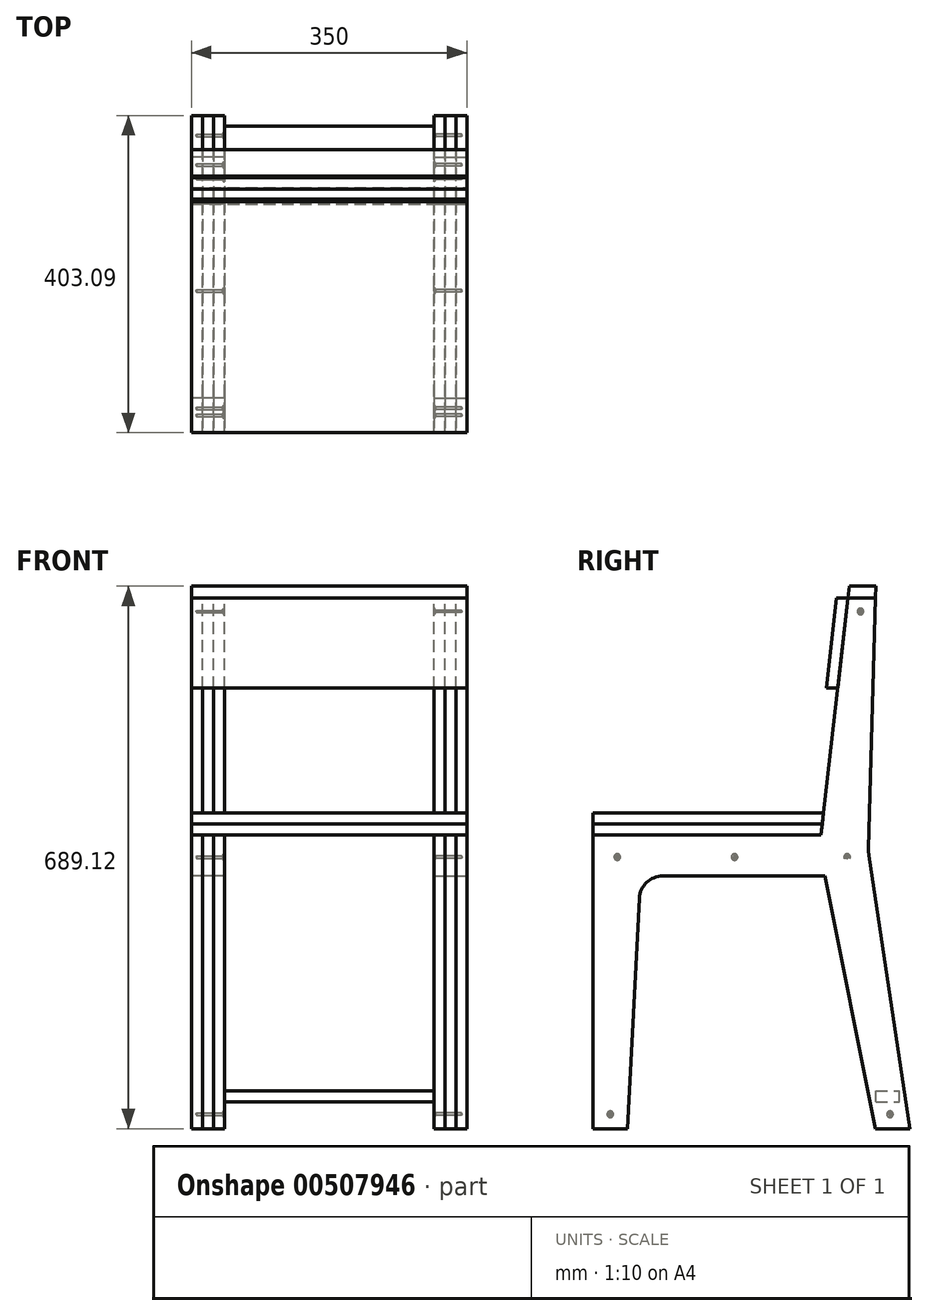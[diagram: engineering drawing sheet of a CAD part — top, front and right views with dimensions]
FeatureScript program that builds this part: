
annotation { "Feature Type Name" : "Feature", "Feature Type Description" : "" }
export const myFeature = defineFeature(function(context is Context, id is Id, definition is map)
    precondition{}
    {
        {
            var Q0;
            Q0=qCreatedBy(makeId("Right.planeOp"),FACE);
            var sketch = newSketch(context, id + "F0", { "sketchPlane" : qUnion([Q0])});
            skLineSegment(sketch, "E0", {"start": v(-65.3, 0) * mm, "end": v(224.7, 0) * mm});
            skLineSegment(sketch, "E1", {"start": v(224.7, 0) * mm, "end": v(258.7, 301.28) * mm});
            skLineSegment(sketch, "E2", {"start": v(258.7, 301.28) * mm, "end": v(293.7, 301.28) * mm});
            skLineSegment(sketch, "E3", {"start": v(337.7, -373) * mm, "end": v(293.7, -373) * mm});
            skLineSegment(sketch, "E4", {"start": v(293.7, -373) * mm, "end": v(229.2, -52) * mm});
            skLineSegment(sketch, "E5", {"start": v(229.2, -52) * mm, "end": v(23.69, -52) * mm});
            skLineSegment(sketch, "E6", {"start": v(-21.3, -373) * mm, "end": v(-65.3, -373) * mm});
            skLineSegment(sketch, "E7", {"start": v(-65.3, -373) * mm, "end": v(-65.3, 0) * mm});
            skPoint(sketch, "E8.visualSharp", {"position": v(-29.5, -52) * mm});
            skLineSegment(sketch, "E9.bottom", {"start": v(-65.3, 0) * mm, "end": v(-29.5, 0) * mm});
            skLineSegment(sketch, "E9.top", {"start": v(-65.3, -373) * mm, "end": v(-21.3, -373) * mm});
            skLineSegment(sketch, "E9.left", {"start": v(-65.3, 0) * mm, "end": v(-65.3, -373) * mm});
            skLineSegment(sketch, "E10", {"start": v(337.7, -373) * mm, "end": v(285.36, -25.8) * mm});
            skLineSegment(sketch, "E11", {"start": v(284.82, -16.95) * mm, "end": v(293.7, 301.28) * mm});
            skLineSegment(sketch, "E12", {"start": v(-6.27, -80.46) * mm, "end": v(-21.3, -373) * mm});
            skPoint(sketch, "E13.visualSharp", {"position": v(-4.8, -52) * mm});
            skArc(sketch, "E13.filletArc", {"start": v(23.69, -52) * mm, "mid": v(3.03, -60.25) * mm, "end": v(-6.27, -80.46) * mm});
            skPoint(sketch, "E14.visualSharp", {"position": v(284.7, -21.4) * mm});
            skArc(sketch, "E14.filletArc", {"start": v(284.82, -16.95) * mm, "mid": v(284.89, -21.38) * mm, "end": v(285.36, -25.8) * mm});
            skSolve(sketch);
        }
        {
            var Q0;
            Q0=qCreatedBy(makeId("Right.planeOp"),FACE);
            var sketch = newSketch(context, id + "F1", { "sketchPlane" : qUnion([Q0])});
            skLineSegment(sketch, "E15", {"start": v(-65.3, 0) * mm, "end": v(224.7, 0) * mm});
            skLineSegment(sketch, "E16", {"start": v(224.7, 0) * mm, "end": v(226.27, 14) * mm});
            skLineSegment(sketch, "E17", {"start": v(226.27, 14) * mm, "end": v(-65.3, 14) * mm});
            skLineSegment(sketch, "E18", {"start": v(-65.3, 14) * mm, "end": v(-65.3, 0) * mm});
            skSolve(sketch);
        }
        {
            var Q0;
            Q0=qCreatedBy(makeId("Right.planeOp"),FACE);
            var sketch = newSketch(context, id + "F2", { "sketchPlane" : qUnion([Q0])});
            skLineSegment(sketch, "E19", {"start": v(-65.3, 14) * mm, "end": v(226.27, 14) * mm});
            skLineSegment(sketch, "E20", {"start": v(226.27, 14) * mm, "end": v(227.85, 28) * mm});
            skLineSegment(sketch, "E21", {"start": v(227.85, 28) * mm, "end": v(-65.4, 28) * mm});
            skLineSegment(sketch, "E22", {"start": v(-65.4, 28) * mm, "end": v(-65.3, 14) * mm});
            skSolve(sketch);
        }
        {
            var Q0;
            Q0=makeQuery(id+"F0.imprint","IMPRINT",FACE,{"disambiguationData":[TD([[makeQuery(id+"F0.imprint","IMPRINT",EDGE,{"derivedFrom":sQuery(id+"F0.wireOp",EDGE,"E0")}),-1.0]])]});
            extrude(context, id + "F3", {"entities" : qUnion([Q0]), "oppositeDirection" : true, "depth" : 14 * mm});
        }
        {
            var Q0;
            Q0=makeQuery(id+"F1.imprint","IMPRINT",FACE,{"disambiguationData":[TD([[makeQuery(id+"F1.imprint","IMPRINT",EDGE,{"derivedFrom":sQuery(id+"F1.wireOp",EDGE,"E15")}),1.0]])]});
            extrude(context, id + "F4", {"entities" : qUnion([Q0]), "oppositeDirection" : true, "depth" : 350 * mm});
        }
        {
            var Q0;
            Q0=makeQuery(id+"F3.opExtrude","SWEPT_BODY",BODY,{"disambiguationData":[OSD([sQuery(id+"F0.wireOp",EDGE,"E0"),sQuery(id+"F0.wireOp",EDGE,"E1"),sQuery(id+"F0.wireOp",EDGE,"E2"),sQuery(id+"F0.wireOp",EDGE,"E3"),sQuery(id+"F0.wireOp",EDGE,"E4"),sQuery(id+"F0.wireOp",EDGE,"E5"),sQuery(id+"F0.wireOp",EDGE,"E9.bottom"),sQuery(id+"F0.wireOp",EDGE,"E9.top"),sQuery(id+"F0.wireOp",EDGE,"E9.left"),sQuery(id+"F0.wireOp",EDGE,"E10"),sQuery(id+"F0.wireOp",EDGE,"E11"),sQuery(id+"F0.wireOp",EDGE,"E12"),sQuery(id+"F0.wireOp",EDGE,"E13.filletArc"),sQuery(id+"F0.wireOp",EDGE,"E14.filletArc")])]});
            transform(context, id + "F5", {"entities" : qUnion([Q0]), "transformType" : TransformType.TRANSLATION_3D, "dx" : -14 * mm, "dy" : 0 * mm, "dz" : 0 * mm, "makeCopy" : true});
        }
        {
            var Q0;
            Q0=makeQuery(id+"F3.opExtrude","SWEPT_BODY",BODY,{"disambiguationData":[OSD([sQuery(id+"F0.wireOp",EDGE,"E0"),sQuery(id+"F0.wireOp",EDGE,"E1"),sQuery(id+"F0.wireOp",EDGE,"E2"),sQuery(id+"F0.wireOp",EDGE,"E3"),sQuery(id+"F0.wireOp",EDGE,"E4"),sQuery(id+"F0.wireOp",EDGE,"E5"),sQuery(id+"F0.wireOp",EDGE,"E9.bottom"),sQuery(id+"F0.wireOp",EDGE,"E9.top"),sQuery(id+"F0.wireOp",EDGE,"E9.left"),sQuery(id+"F0.wireOp",EDGE,"E10"),sQuery(id+"F0.wireOp",EDGE,"E11"),sQuery(id+"F0.wireOp",EDGE,"E12"),sQuery(id+"F0.wireOp",EDGE,"E13.filletArc"),sQuery(id+"F0.wireOp",EDGE,"E14.filletArc")])]});
            transform(context, id + "F6", {"entities" : qUnion([Q0]), "transformType" : TransformType.TRANSLATION_3D, "dx" : -28 * mm, "dy" : 0 * mm, "dz" : 0 * mm, "makeCopy" : true});
        }
        {
            var Q0;
            Q0=makeQuery(id+"F2.imprint","IMPRINT",FACE,{"disambiguationData":[TD([[makeQuery(id+"F2.imprint","IMPRINT",EDGE,{"derivedFrom":sQuery(id+"F2.wireOp",EDGE,"E19")}),1.0]])]});
            extrude(context, id + "F7", {"entities" : qUnion([Q0]), "oppositeDirection" : true, "depth" : 350 * mm});
        }
        {
            var Q0;
            Q0=makeQuery(id+"F3.opExtrude","SWEPT_BODY",BODY,{"disambiguationData":[OSD([sQuery(id+"F0.wireOp",EDGE,"E0"),sQuery(id+"F0.wireOp",EDGE,"E1"),sQuery(id+"F0.wireOp",EDGE,"E2"),sQuery(id+"F0.wireOp",EDGE,"E3"),sQuery(id+"F0.wireOp",EDGE,"E4"),sQuery(id+"F0.wireOp",EDGE,"E5"),sQuery(id+"F0.wireOp",EDGE,"E9.bottom"),sQuery(id+"F0.wireOp",EDGE,"E9.top"),sQuery(id+"F0.wireOp",EDGE,"E9.left"),sQuery(id+"F0.wireOp",EDGE,"E10"),sQuery(id+"F0.wireOp",EDGE,"E11"),sQuery(id+"F0.wireOp",EDGE,"E12"),sQuery(id+"F0.wireOp",EDGE,"E13.filletArc"),sQuery(id+"F0.wireOp",EDGE,"E14.filletArc")])]});
            transform(context, id + "F8", {"entities" : qUnion([Q0]), "transformType" : TransformType.TRANSLATION_3D, "dx" : -336 * mm, "dy" : 0 * mm, "dz" : 0 * mm, "makeCopy" : true});
        }
        {
            var Q0;
            Q0=makeQuery(id+"F8.opPattern","COPY",BODY,{"derivedFrom":makeQuery(id+"F3.opExtrude","SWEPT_BODY",BODY,{"disambiguationData":[OSD([sQuery(id+"F0.wireOp",EDGE,"E0"),sQuery(id+"F0.wireOp",EDGE,"E1"),sQuery(id+"F0.wireOp",EDGE,"E2"),sQuery(id+"F0.wireOp",EDGE,"E3"),sQuery(id+"F0.wireOp",EDGE,"E4"),sQuery(id+"F0.wireOp",EDGE,"E5"),sQuery(id+"F0.wireOp",EDGE,"E9.bottom"),sQuery(id+"F0.wireOp",EDGE,"E9.top"),sQuery(id+"F0.wireOp",EDGE,"E9.left"),sQuery(id+"F0.wireOp",EDGE,"E10"),sQuery(id+"F0.wireOp",EDGE,"E11"),sQuery(id+"F0.wireOp",EDGE,"E12"),sQuery(id+"F0.wireOp",EDGE,"E13.filletArc"),sQuery(id+"F0.wireOp",EDGE,"E14.filletArc")])]}),"instanceName":"1"});
            transform(context, id + "F9", {"entities" : qUnion([Q0]), "transformType" : TransformType.TRANSLATION_3D, "dx" : 14 * mm, "dy" : 0 * mm, "dz" : 0 * mm, "makeCopy" : true});
        }
        {
            var Q0;
            Q0=makeQuery(id+"F9.opPattern","COPY",BODY,{"derivedFrom":makeQuery(id+"F8.opPattern","COPY",BODY,{"derivedFrom":makeQuery(id+"F3.opExtrude","SWEPT_BODY",BODY,{"disambiguationData":[OSD([sQuery(id+"F0.wireOp",EDGE,"E0"),sQuery(id+"F0.wireOp",EDGE,"E1"),sQuery(id+"F0.wireOp",EDGE,"E2"),sQuery(id+"F0.wireOp",EDGE,"E3"),sQuery(id+"F0.wireOp",EDGE,"E4"),sQuery(id+"F0.wireOp",EDGE,"E5"),sQuery(id+"F0.wireOp",EDGE,"E9.bottom"),sQuery(id+"F0.wireOp",EDGE,"E9.top"),sQuery(id+"F0.wireOp",EDGE,"E9.left"),sQuery(id+"F0.wireOp",EDGE,"E10"),sQuery(id+"F0.wireOp",EDGE,"E11"),sQuery(id+"F0.wireOp",EDGE,"E12"),sQuery(id+"F0.wireOp",EDGE,"E13.filletArc"),sQuery(id+"F0.wireOp",EDGE,"E14.filletArc")])]}),"instanceName":"1"}),"instanceName":"1"});
            transform(context, id + "F10", {"entities" : qUnion([Q0]), "transformType" : TransformType.TRANSLATION_3D, "dx" : 14 * mm, "dy" : 0 * mm, "dz" : 0 * mm, "makeCopy" : true});
        }
        {
            var Q0;
            Q0=qCreatedBy(makeId("Right.planeOp"),FACE);
            var sketch = newSketch(context, id + "F11", { "sketchPlane" : qUnion([Q0])});
            skLineSegment(sketch, "E23", {"start": v(293.7, 301.28) * mm, "end": v(294.1, 316.12) * mm});
            skLineSegment(sketch, "E24", {"start": v(294.1, 316.12) * mm, "end": v(260.37, 316.12) * mm});
            skLineSegment(sketch, "E25", {"start": v(260.37, 316.12) * mm, "end": v(258.7, 301.28) * mm});
            skLineSegment(sketch, "E26", {"start": v(258.7, 301.28) * mm, "end": v(293.7, 301.28) * mm});
            skSolve(sketch);
        }
        {
            var Q0;
            Q0 = qSketchRegion(id + "F11", true);
            extrude(context, id + "F12", {"entities" : qUnion([Q0]), "oppositeDirection" : true, "depth" : 350 * mm});
        }
        {
            var Q0;
            Q0=qCreatedBy(makeId("Front.planeOp"),FACE);
            var sketch = newSketch(context, id + "F13", { "sketchPlane" : qUnion([Q0])});
            skLineSegment(sketch, "E27.bottom", {"start": v(-308, -332.73) * mm, "end": v(-42, -332.73) * mm});
            skLineSegment(sketch, "E27.top", {"start": v(-308, -318.73) * mm, "end": v(-42, -318.73) * mm});
            skLineSegment(sketch, "E27.left", {"start": v(-308, -332.73) * mm, "end": v(-308, -318.73) * mm});
            skLineSegment(sketch, "E27.right", {"start": v(-42, -332.73) * mm, "end": v(-42, -318.73) * mm});
            skSolve(sketch);
        }
        {
            var Q0;
            Q0 = qSketchRegion(id + "F13", true);
            extrude(context, id + "F14", {"entities" : qUnion([Q0]), "depth" : 30 * mm});
        }
        {
            var Q0;
            Q0=makeQuery(id+"F14.opExtrude","SWEPT_BODY",BODY,{"disambiguationData":[OSD([sQuery(id+"F13.wireOp",EDGE,"E27.bottom"),sQuery(id+"F13.wireOp",EDGE,"E27.top"),sQuery(id+"F13.wireOp",EDGE,"E27.left"),sQuery(id+"F13.wireOp",EDGE,"E27.right")])]});
            transform(context, id + "F15", {"entities" : qUnion([Q0]), "transformType" : TransformType.TRANSLATION_3D, "dx" : 0 * mm, "dy" : -27 * mm, "dz" : 0 * mm, "makeCopy" : false});
        }
        {
            var Q0;
            Q0=makeQuery(id+"F14.opExtrude","SWEPT_BODY",BODY,{"disambiguationData":[OSD([sQuery(id+"F13.wireOp",EDGE,"E27.bottom"),sQuery(id+"F13.wireOp",EDGE,"E27.top"),sQuery(id+"F13.wireOp",EDGE,"E27.left"),sQuery(id+"F13.wireOp",EDGE,"E27.right")])]});
            transform(context, id + "F16", {"entities" : qUnion([Q0]), "transformType" : TransformType.TRANSLATION_3D, "dx" : 0 * mm, "dy" : 352 * mm, "dz" : -17 * mm, "makeCopy" : false});
        }
        {
            var Q0;
            Q0=makeQuery(id+"F14.opExtrude","SWEPT_BODY",BODY,{"disambiguationData":[OSD([sQuery(id+"F13.wireOp",EDGE,"E27.bottom"),sQuery(id+"F13.wireOp",EDGE,"E27.top"),sQuery(id+"F13.wireOp",EDGE,"E27.left"),sQuery(id+"F13.wireOp",EDGE,"E27.right")])]});
            transform(context, id + "F17", {"entities" : qUnion([Q0]), "transformType" : TransformType.TRANSLATION_3D, "dx" : 0 * mm, "dy" : -1 * mm, "dz" : 11 * mm, "makeCopy" : false});
        }
        {
            var Q0;
            Q0=qCreatedBy(makeId("Top.planeOp"),FACE);
            var sketch = newSketch(context, id + "F18", { "sketchPlane" : qUnion([Q0])});
            skLineSegment(sketch, "E28.bottom", {"start": v(-432.94, -234.27) * mm, "end": v(-390.94, -234.27) * mm});
            skLineSegment(sketch, "E28.top", {"start": v(-432.94, -190.27) * mm, "end": v(-390.94, -190.27) * mm});
            skLineSegment(sketch, "E28.left", {"start": v(-432.94, -234.27) * mm, "end": v(-432.94, -190.27) * mm});
            skLineSegment(sketch, "E28.right", {"start": v(-390.94, -234.27) * mm, "end": v(-390.94, -190.27) * mm});
            skSolve(sketch);
        }
        {
            var Q0;
            Q0=makeQuery(id+"F18.imprint","IMPRINT",FACE,{"disambiguationData":[TD([[makeQuery(id+"F18.imprint","IMPRINT",EDGE,{"derivedFrom":sQuery(id+"F18.wireOp",EDGE,"E28.bottom")}),1.0]])]});
            extrude(context, id + "F19", {"entities" : qUnion([Q0]), "depth" : 4 * mm});
        }
        {
            var Q0;
            Q0=makeQuery(id+"F19.opExtrude","SWEPT_BODY",BODY,{"disambiguationData":[OSD([sQuery(id+"F18.wireOp",EDGE,"E28.bottom"),sQuery(id+"F18.wireOp",EDGE,"E28.top"),sQuery(id+"F18.wireOp",EDGE,"E28.left"),sQuery(id+"F18.wireOp",EDGE,"E28.right")])]});
            transform(context, id + "F20", {"entities" : qUnion([Q0]), "transformType" : TransformType.TRANSLATION_3D, "dx" : 82.9 * mm, "dy" : 168.9 * mm, "dz" : -377 * mm, "makeCopy" : false});
        }
        {
            var Q0;
            Q0=makeQuery(id+"F19.opExtrude","SWEPT_BODY",BODY,{"disambiguationData":[OSD([sQuery(id+"F18.wireOp",EDGE,"E28.bottom"),sQuery(id+"F18.wireOp",EDGE,"E28.top"),sQuery(id+"F18.wireOp",EDGE,"E28.left"),sQuery(id+"F18.wireOp",EDGE,"E28.right")])]});
            transform(context, id + "F21", {"entities" : qUnion([Q0]), "transformType" : TransformType.TRANSLATION_3D, "dx" : 0 * mm, "dy" : 359.2 * mm, "dz" : 0 * mm, "makeCopy" : true});
        }
        {
            var Q0;
            Q0=makeQuery(id+"F19.opExtrude","SWEPT_BODY",BODY,{"disambiguationData":[OSD([sQuery(id+"F18.wireOp",EDGE,"E28.bottom"),sQuery(id+"F18.wireOp",EDGE,"E28.top"),sQuery(id+"F18.wireOp",EDGE,"E28.left"),sQuery(id+"F18.wireOp",EDGE,"E28.right")])]});
            transform(context, id + "F22", {"entities" : qUnion([Q0]), "transformType" : TransformType.TRANSLATION_3D, "dx" : 308.2 * mm, "dy" : 0 * mm, "dz" : 0 * mm, "makeCopy" : true});
        }
        {
            var Q0;
            Q0=makeQuery(id+"F21.opPattern","COPY",BODY,{"derivedFrom":makeQuery(id+"F19.opExtrude","SWEPT_BODY",BODY,{"disambiguationData":[OSD([sQuery(id+"F18.wireOp",EDGE,"E28.bottom"),sQuery(id+"F18.wireOp",EDGE,"E28.top"),sQuery(id+"F18.wireOp",EDGE,"E28.left"),sQuery(id+"F18.wireOp",EDGE,"E28.right")])]}),"instanceName":"1"});
            transform(context, id + "F23", {"entities" : qUnion([Q0]), "transformType" : TransformType.TRANSLATION_3D, "dx" : 308.1 * mm, "dy" : 0 * mm, "dz" : 0 * mm, "makeCopy" : true});
        }
        {
            var Q0;
            Q0=makeQuery(id+"F19.opExtrude","SWEPT_BODY",BODY,{"disambiguationData":[OSD([sQuery(id+"F18.wireOp",EDGE,"E28.bottom"),sQuery(id+"F18.wireOp",EDGE,"E28.top"),sQuery(id+"F18.wireOp",EDGE,"E28.left"),sQuery(id+"F18.wireOp",EDGE,"E28.right")])]});
            var Q1;
            Q1=makeQuery(id+"F21.opPattern","COPY",BODY,{"derivedFrom":makeQuery(id+"F19.opExtrude","SWEPT_BODY",BODY,{"disambiguationData":[OSD([sQuery(id+"F18.wireOp",EDGE,"E28.bottom"),sQuery(id+"F18.wireOp",EDGE,"E28.top"),sQuery(id+"F18.wireOp",EDGE,"E28.left"),sQuery(id+"F18.wireOp",EDGE,"E28.right")])]}),"instanceName":"1"});
            var Q2;
            Q2=makeQuery(id+"F22.opPattern","COPY",BODY,{"derivedFrom":makeQuery(id+"F19.opExtrude","SWEPT_BODY",BODY,{"disambiguationData":[OSD([sQuery(id+"F18.wireOp",EDGE,"E28.bottom"),sQuery(id+"F18.wireOp",EDGE,"E28.top"),sQuery(id+"F18.wireOp",EDGE,"E28.left"),sQuery(id+"F18.wireOp",EDGE,"E28.right")])]}),"instanceName":"1"});
            var Q3;
            Q3=makeQuery(id+"F23.opPattern","COPY",BODY,{"derivedFrom":makeQuery(id+"F21.opPattern","COPY",BODY,{"derivedFrom":makeQuery(id+"F19.opExtrude","SWEPT_BODY",BODY,{"disambiguationData":[OSD([sQuery(id+"F18.wireOp",EDGE,"E28.bottom"),sQuery(id+"F18.wireOp",EDGE,"E28.top"),sQuery(id+"F18.wireOp",EDGE,"E28.left"),sQuery(id+"F18.wireOp",EDGE,"E28.right")])]}),"instanceName":"1"}),"instanceName":"1"});
            deleteBodies(context, id + "F24", {"entities" : qUnion([Q0, Q1, Q2, Q3])});
        }
        {
            var Q0;
            Q0=qCreatedBy(makeId("Right.planeOp"),FACE);
            var sketch = newSketch(context, id + "F25", { "sketchPlane" : qUnion([Q0])});
            skLineSegment(sketch, "E29", {"start": v(260.32, 316.17) * mm, "end": v(247.36, 201.4) * mm});
            skLineSegment(sketch, "E30", {"start": v(247.36, 201.4) * mm, "end": v(232.9, 201.4) * mm});
            skLineSegment(sketch, "E31", {"start": v(232.9, 201.4) * mm, "end": v(245.85, 316.17) * mm});
            skLineSegment(sketch, "E32", {"start": v(245.85, 316.17) * mm, "end": v(260.32, 316.17) * mm});
            skSolve(sketch);
        }
        {
            var Q0;
            Q0=makeQuery(id+"F25.imprint","IMPRINT",FACE,{"disambiguationData":[TD([[makeQuery(id+"F25.imprint","IMPRINT",EDGE,{"derivedFrom":sQuery(id+"F25.wireOp",EDGE,"E29")}),-1.0]])]});
            extrude(context, id + "F26", {"entities" : qUnion([Q0]), "oppositeDirection" : true, "depth" : 350 * mm});
        }
        {
            var Q0;
            Q0=makeQuery(id+"F26.opExtrude","SWEPT_BODY",BODY,{"disambiguationData":[OSD([sQuery(id+"F25.wireOp",EDGE,"E29"),sQuery(id+"F25.wireOp",EDGE,"E30"),sQuery(id+"F25.wireOp",EDGE,"E31"),sQuery(id+"F25.wireOp",EDGE,"E32")])]});
            transform(context, id + "F27", {"entities" : qUnion([Q0]), "transformType" : TransformType.TRANSLATION_3D, "dx" : 0 * mm, "dy" : -1.62 * mm, "dz" : -14.9 * mm, "makeCopy" : false});
        }
        {
            var Q0;
            Q0=qCreatedBy(makeId("Right.planeOp"),FACE);
            var sketch = newSketch(context, id + "F28", { "sketchPlane" : qUnion([Q0])});
            skCircle(sketch, "E33", {"center": v(-65.3, 0) * mm, "radius": 4 * mm});
            skSolve(sketch);
        }
        {
            var Q0;
            Q0=makeQuery(id+"F28.imprint","IMPRINT",FACE,{"disambiguationData":[TD([[makeQuery(id+"F28.imprint","IMPRINT",EDGE,{"derivedFrom":sQuery(id+"F28.wireOp",EDGE,"E33")}),1.0]])]});
            extrude(context, id + "F29", {"entities" : qUnion([Q0]), "depth" : 1 * mm});
        }
        {
            var Q0;
            Q0=makeQuery(id+"F29.opExtrude","SWEPT_BODY",BODY,{"disambiguationData":[OSD([sQuery(id+"F28.wireOp",EDGE,"E33")])]});
            transform(context, id + "F30", {"entities" : qUnion([Q0]), "transformType" : TransformType.TRANSLATION_3D, "dx" : -43 * mm, "dy" : 31 * mm, "dz" : -28 * mm, "makeCopy" : false});
        }
        {
            var Q0;
            Q0=makeQuery(id+"F29.opExtrude","SWEPT_BODY",BODY,{"disambiguationData":[OSD([sQuery(id+"F28.wireOp",EDGE,"E33")])]});
            transform(context, id + "F31", {"entities" : qUnion([Q0]), "transformType" : TransformType.TRANSLATION_3D, "dx" : 0 * mm, "dy" : 142 * mm, "dz" : 0 * mm, "makeCopy" : true});
        }
        {
            var Q0;
            Q0=makeQuery(id+"F31.opPattern","COPY",BODY,{"derivedFrom":makeQuery(id+"F29.opExtrude","SWEPT_BODY",BODY,{"disambiguationData":[OSD([sQuery(id+"F28.wireOp",EDGE,"E33")])]}),"instanceName":"1"});
            transform(context, id + "F32", {"entities" : qUnion([Q0]), "transformType" : TransformType.TRANSLATION_3D, "dx" : 0 * mm, "dy" : 150 * mm, "dz" : 0 * mm, "makeCopy" : true});
        }
        {
            var Q0;
            Q0=makeQuery(id+"F31.opPattern","COPY",BODY,{"derivedFrom":makeQuery(id+"F29.opExtrude","SWEPT_BODY",BODY,{"disambiguationData":[OSD([sQuery(id+"F28.wireOp",EDGE,"E33")])]}),"instanceName":"1"});
            transform(context, id + "F33", {"entities" : qUnion([Q0]), "transformType" : TransformType.TRANSLATION_3D, "dx" : 0 * mm, "dy" : 7 * mm, "dz" : 0 * mm, "makeCopy" : false});
        }
        {
            var Q0;
            Q0=makeQuery(id+"F32.opPattern","COPY",BODY,{"derivedFrom":makeQuery(id+"F31.opPattern","COPY",BODY,{"derivedFrom":makeQuery(id+"F29.opExtrude","SWEPT_BODY",BODY,{"disambiguationData":[OSD([sQuery(id+"F28.wireOp",EDGE,"E33")])]}),"instanceName":"1"}),"instanceName":"1"});
            transform(context, id + "F34", {"entities" : qUnion([Q0]), "transformType" : TransformType.TRANSLATION_3D, "dx" : 0 * mm, "dy" : 17 * mm, "dz" : 312 * mm, "makeCopy" : true});
        }
        {
            var Q0;
            Q0=makeQuery(id+"F32.opPattern","COPY",BODY,{"derivedFrom":makeQuery(id+"F31.opPattern","COPY",BODY,{"derivedFrom":makeQuery(id+"F29.opExtrude","SWEPT_BODY",BODY,{"disambiguationData":[OSD([sQuery(id+"F28.wireOp",EDGE,"E33")])]}),"instanceName":"1"}),"instanceName":"1"});
            transform(context, id + "F35", {"entities" : qUnion([Q0]), "transformType" : TransformType.TRANSLATION_3D, "dx" : 0 * mm, "dy" : 54.5 * mm, "dz" : -326.7 * mm, "makeCopy" : true});
        }
        {
            var Q0;
            Q0=makeQuery(id+"F35.opPattern","COPY",BODY,{"derivedFrom":makeQuery(id+"F32.opPattern","COPY",BODY,{"derivedFrom":makeQuery(id+"F31.opPattern","COPY",BODY,{"derivedFrom":makeQuery(id+"F29.opExtrude","SWEPT_BODY",BODY,{"disambiguationData":[OSD([sQuery(id+"F28.wireOp",EDGE,"E33")])]}),"instanceName":"1"}),"instanceName":"1"}),"instanceName":"1"});
            transform(context, id + "F36", {"entities" : qUnion([Q0]), "transformType" : TransformType.TRANSLATION_3D, "dx" : 0 * mm, "dy" : -355.4 * mm, "dz" : 0 * mm, "makeCopy" : true});
        }
        {
            var Q0;
            Q0=makeQuery(id+"F6.opPattern","COPY",FACE,{"derivedFrom":makeQuery(id+"F3.opExtrude","CAP_FACE",FACE,{"disambiguationData":[OSD([sQuery(id+"F0.wireOp",EDGE,"E0"),sQuery(id+"F0.wireOp",EDGE,"E1"),sQuery(id+"F0.wireOp",EDGE,"E2"),sQuery(id+"F0.wireOp",EDGE,"E3"),sQuery(id+"F0.wireOp",EDGE,"E4"),sQuery(id+"F0.wireOp",EDGE,"E5"),sQuery(id+"F0.wireOp",EDGE,"E9.bottom"),sQuery(id+"F0.wireOp",EDGE,"E9.top"),sQuery(id+"F0.wireOp",EDGE,"E9.left"),sQuery(id+"F0.wireOp",EDGE,"E10"),sQuery(id+"F0.wireOp",EDGE,"E11"),sQuery(id+"F0.wireOp",EDGE,"E12"),sQuery(id+"F0.wireOp",EDGE,"E13.filletArc"),sQuery(id+"F0.wireOp",EDGE,"E14.filletArc")])],"isStart":false}),"instanceName":"1"});
            var sketch = newSketch(context, id + "F37", { "sketchPlane" : qUnion([Q0])});
            skCircle(sketch, "E34.0", {"center": v(-257.7, -28) * mm, "radius": 4 * mm});
            skSolve(sketch);
        }
        {
            var Q0;
            Q0=sQuery(id+"F37.wireOp",VERTEX,"E34.0.center");
            var Q1;
            Q1=makeQuery(id+"F5.opPattern","COPY",BODY,{"derivedFrom":makeQuery(id+"F3.opExtrude","SWEPT_BODY",BODY,{"disambiguationData":[OSD([sQuery(id+"F0.wireOp",EDGE,"E0"),sQuery(id+"F0.wireOp",EDGE,"E1"),sQuery(id+"F0.wireOp",EDGE,"E2"),sQuery(id+"F0.wireOp",EDGE,"E3"),sQuery(id+"F0.wireOp",EDGE,"E4"),sQuery(id+"F0.wireOp",EDGE,"E5"),sQuery(id+"F0.wireOp",EDGE,"E9.bottom"),sQuery(id+"F0.wireOp",EDGE,"E9.top"),sQuery(id+"F0.wireOp",EDGE,"E9.left"),sQuery(id+"F0.wireOp",EDGE,"E10"),sQuery(id+"F0.wireOp",EDGE,"E11"),sQuery(id+"F0.wireOp",EDGE,"E12"),sQuery(id+"F0.wireOp",EDGE,"E13.filletArc"),sQuery(id+"F0.wireOp",EDGE,"E14.filletArc")])]}),"instanceName":"1"});
            var Q2;
            Q2=makeQuery(id+"F6.opPattern","COPY",BODY,{"derivedFrom":makeQuery(id+"F3.opExtrude","SWEPT_BODY",BODY,{"disambiguationData":[OSD([sQuery(id+"F0.wireOp",EDGE,"E0"),sQuery(id+"F0.wireOp",EDGE,"E1"),sQuery(id+"F0.wireOp",EDGE,"E2"),sQuery(id+"F0.wireOp",EDGE,"E3"),sQuery(id+"F0.wireOp",EDGE,"E4"),sQuery(id+"F0.wireOp",EDGE,"E5"),sQuery(id+"F0.wireOp",EDGE,"E9.bottom"),sQuery(id+"F0.wireOp",EDGE,"E9.top"),sQuery(id+"F0.wireOp",EDGE,"E9.left"),sQuery(id+"F0.wireOp",EDGE,"E10"),sQuery(id+"F0.wireOp",EDGE,"E11"),sQuery(id+"F0.wireOp",EDGE,"E12"),sQuery(id+"F0.wireOp",EDGE,"E13.filletArc"),sQuery(id+"F0.wireOp",EDGE,"E14.filletArc")])]}),"instanceName":"1"});
            var Q3;
            Q3=makeQuery(id+"F3.opExtrude","SWEPT_BODY",BODY,{"disambiguationData":[OSD([sQuery(id+"F0.wireOp",EDGE,"E0"),sQuery(id+"F0.wireOp",EDGE,"E1"),sQuery(id+"F0.wireOp",EDGE,"E2"),sQuery(id+"F0.wireOp",EDGE,"E3"),sQuery(id+"F0.wireOp",EDGE,"E4"),sQuery(id+"F0.wireOp",EDGE,"E5"),sQuery(id+"F0.wireOp",EDGE,"E9.bottom"),sQuery(id+"F0.wireOp",EDGE,"E9.top"),sQuery(id+"F0.wireOp",EDGE,"E9.left"),sQuery(id+"F0.wireOp",EDGE,"E10"),sQuery(id+"F0.wireOp",EDGE,"E11"),sQuery(id+"F0.wireOp",EDGE,"E12"),sQuery(id+"F0.wireOp",EDGE,"E13.filletArc"),sQuery(id+"F0.wireOp",EDGE,"E14.filletArc")])]});
            hole(context, id + "F38", {"style" : HoleStyle.SIMPLE, "endStyle" : HoleEndStyle.BLIND_IN_LAST, "holeDiameter" : 3 * mm, "tapDrillDiameter" : 3 * mm, "holeDepth" : 7 * mm, "isTappedThrough" : true, "tappedDepth" : 12 * mm, "tapClearance" : 3, "locations" : qUnion([Q0]), "scope" : qUnion([Q1, Q2, Q3])});
        }
        {
            var Q0;
            Q0=sQuery(id+"F37.wireOp",VERTEX,"E34.0.center");
            var Q1;
            Q1=makeQuery(id+"F6.opPattern","COPY",BODY,{"derivedFrom":makeQuery(id+"F3.opExtrude","SWEPT_BODY",BODY,{"disambiguationData":[OSD([sQuery(id+"F0.wireOp",EDGE,"E0"),sQuery(id+"F0.wireOp",EDGE,"E1"),sQuery(id+"F0.wireOp",EDGE,"E2"),sQuery(id+"F0.wireOp",EDGE,"E3"),sQuery(id+"F0.wireOp",EDGE,"E4"),sQuery(id+"F0.wireOp",EDGE,"E5"),sQuery(id+"F0.wireOp",EDGE,"E9.bottom"),sQuery(id+"F0.wireOp",EDGE,"E9.top"),sQuery(id+"F0.wireOp",EDGE,"E9.left"),sQuery(id+"F0.wireOp",EDGE,"E10"),sQuery(id+"F0.wireOp",EDGE,"E11"),sQuery(id+"F0.wireOp",EDGE,"E12"),sQuery(id+"F0.wireOp",EDGE,"E13.filletArc"),sQuery(id+"F0.wireOp",EDGE,"E14.filletArc")])]}),"instanceName":"1"});
            hole(context, id + "F39", {"style" : HoleStyle.SIMPLE, "endStyle" : HoleEndStyle.BLIND, "holeDiameter" : 8 * mm, "holeDepth" : 1 * mm, "isTappedThrough" : true, "tappedDepth" : 12 * mm, "tapClearance" : 3, "locations" : qUnion([Q0]), "scope" : qUnion([Q1])});
        }
        {
            var Q0;
            Q0=makeQuery(id+"F32.opPattern","COPY",BODY,{"derivedFrom":makeQuery(id+"F31.opPattern","COPY",BODY,{"derivedFrom":makeQuery(id+"F29.opExtrude","SWEPT_BODY",BODY,{"disambiguationData":[OSD([sQuery(id+"F28.wireOp",EDGE,"E33")])]}),"instanceName":"1"}),"instanceName":"1"});
            transform(context, id + "F40", {"entities" : qUnion([Q0]), "transformType" : TransformType.TRANSLATION_3D, "dx" : 1 * mm, "dy" : 0 * mm, "dz" : 0 * mm, "makeCopy" : false});
        }
        {
            var Q0;
            Q0=makeQuery(id+"F31.opPattern","COPY",FACE,{"derivedFrom":makeQuery(id+"F29.opExtrude","CAP_FACE",FACE,{"disambiguationData":[OSD([sQuery(id+"F28.wireOp",EDGE,"E33")])],"isStart":true}),"instanceName":"1"});
            var sketch = newSketch(context, id + "F41", { "sketchPlane" : qUnion([Q0])});
            skCircle(sketch, "E35.0", {"center": v(-114.7, -28) * mm, "radius": 4 * mm});
            skCircle(sketch, "E36.0", {"center": v(34.3, -28) * mm, "radius": 4 * mm});
            skCircle(sketch, "E37.0", {"center": v(43.2, -354.7) * mm, "radius": 4 * mm});
            skCircle(sketch, "E38.0", {"center": v(-312.2, -354.7) * mm, "radius": 4 * mm});
            skCircle(sketch, "E39.0.0", {"center": v(-274.7, 284) * mm, "radius": 4 * mm});
            skSolve(sketch);
        }
        {
            var Q0;
            Q0=sQuery(id+"F41.wireOp",VERTEX,"E39.0.0.center");
            var Q1;
            Q1=sQuery(id+"F41.wireOp",VERTEX,"E35.0.center");
            var Q2;
            Q2=sQuery(id+"F41.wireOp",VERTEX,"E36.0.center");
            var Q3;
            Q3=sQuery(id+"F41.wireOp",VERTEX,"E38.0.center");
            var Q4;
            Q4=sQuery(id+"F41.wireOp",VERTEX,"E37.0.center");
            var Q5;
            Q5=makeQuery(id+"F6.opPattern","COPY",BODY,{"derivedFrom":makeQuery(id+"F3.opExtrude","SWEPT_BODY",BODY,{"disambiguationData":[OSD([sQuery(id+"F0.wireOp",EDGE,"E0"),sQuery(id+"F0.wireOp",EDGE,"E1"),sQuery(id+"F0.wireOp",EDGE,"E2"),sQuery(id+"F0.wireOp",EDGE,"E3"),sQuery(id+"F0.wireOp",EDGE,"E4"),sQuery(id+"F0.wireOp",EDGE,"E5"),sQuery(id+"F0.wireOp",EDGE,"E9.bottom"),sQuery(id+"F0.wireOp",EDGE,"E9.top"),sQuery(id+"F0.wireOp",EDGE,"E9.left"),sQuery(id+"F0.wireOp",EDGE,"E10"),sQuery(id+"F0.wireOp",EDGE,"E11"),sQuery(id+"F0.wireOp",EDGE,"E12"),sQuery(id+"F0.wireOp",EDGE,"E13.filletArc"),sQuery(id+"F0.wireOp",EDGE,"E14.filletArc")])]}),"instanceName":"1"});
            var Q6;
            Q6=makeQuery(id+"F5.opPattern","COPY",BODY,{"derivedFrom":makeQuery(id+"F3.opExtrude","SWEPT_BODY",BODY,{"disambiguationData":[OSD([sQuery(id+"F0.wireOp",EDGE,"E0"),sQuery(id+"F0.wireOp",EDGE,"E1"),sQuery(id+"F0.wireOp",EDGE,"E2"),sQuery(id+"F0.wireOp",EDGE,"E3"),sQuery(id+"F0.wireOp",EDGE,"E4"),sQuery(id+"F0.wireOp",EDGE,"E5"),sQuery(id+"F0.wireOp",EDGE,"E9.bottom"),sQuery(id+"F0.wireOp",EDGE,"E9.top"),sQuery(id+"F0.wireOp",EDGE,"E9.left"),sQuery(id+"F0.wireOp",EDGE,"E10"),sQuery(id+"F0.wireOp",EDGE,"E11"),sQuery(id+"F0.wireOp",EDGE,"E12"),sQuery(id+"F0.wireOp",EDGE,"E13.filletArc"),sQuery(id+"F0.wireOp",EDGE,"E14.filletArc")])]}),"instanceName":"1"});
            var Q7;
            Q7=makeQuery(id+"F3.opExtrude","SWEPT_BODY",BODY,{"disambiguationData":[OSD([sQuery(id+"F0.wireOp",EDGE,"E0"),sQuery(id+"F0.wireOp",EDGE,"E1"),sQuery(id+"F0.wireOp",EDGE,"E2"),sQuery(id+"F0.wireOp",EDGE,"E3"),sQuery(id+"F0.wireOp",EDGE,"E4"),sQuery(id+"F0.wireOp",EDGE,"E5"),sQuery(id+"F0.wireOp",EDGE,"E9.bottom"),sQuery(id+"F0.wireOp",EDGE,"E9.top"),sQuery(id+"F0.wireOp",EDGE,"E9.left"),sQuery(id+"F0.wireOp",EDGE,"E10"),sQuery(id+"F0.wireOp",EDGE,"E11"),sQuery(id+"F0.wireOp",EDGE,"E12"),sQuery(id+"F0.wireOp",EDGE,"E13.filletArc"),sQuery(id+"F0.wireOp",EDGE,"E14.filletArc")])]});
            hole(context, id + "F42", {"style" : HoleStyle.SIMPLE, "endStyle" : HoleEndStyle.BLIND_IN_LAST, "holeDiameter" : 3 * mm, "tapDrillDiameter" : 3 * mm, "holeDepth" : 7 * mm, "isTappedThrough" : true, "tappedDepth" : 12 * mm, "tapClearance" : 3, "locations" : qUnion([Q0, Q1, Q2, Q3, Q4]), "scope" : qUnion([Q5, Q6, Q7])});
        }
        {
            var Q0;
            Q0=sQuery(id+"F41.wireOp",VERTEX,"E39.0.0.center");
            var Q1;
            Q1=sQuery(id+"F41.wireOp",VERTEX,"E35.0.center");
            var Q2;
            Q2=sQuery(id+"F41.wireOp",VERTEX,"E36.0.center");
            var Q3;
            Q3=sQuery(id+"F41.wireOp",VERTEX,"E37.0.center");
            var Q4;
            Q4=sQuery(id+"F41.wireOp",VERTEX,"E38.0.center");
            var Q5;
            Q5=makeQuery(id+"F6.opPattern","COPY",BODY,{"derivedFrom":makeQuery(id+"F3.opExtrude","SWEPT_BODY",BODY,{"disambiguationData":[OSD([sQuery(id+"F0.wireOp",EDGE,"E0"),sQuery(id+"F0.wireOp",EDGE,"E1"),sQuery(id+"F0.wireOp",EDGE,"E2"),sQuery(id+"F0.wireOp",EDGE,"E3"),sQuery(id+"F0.wireOp",EDGE,"E4"),sQuery(id+"F0.wireOp",EDGE,"E5"),sQuery(id+"F0.wireOp",EDGE,"E9.bottom"),sQuery(id+"F0.wireOp",EDGE,"E9.top"),sQuery(id+"F0.wireOp",EDGE,"E9.left"),sQuery(id+"F0.wireOp",EDGE,"E10"),sQuery(id+"F0.wireOp",EDGE,"E11"),sQuery(id+"F0.wireOp",EDGE,"E12"),sQuery(id+"F0.wireOp",EDGE,"E13.filletArc"),sQuery(id+"F0.wireOp",EDGE,"E14.filletArc")])]}),"instanceName":"1"});
            hole(context, id + "F43", {"style" : HoleStyle.SIMPLE, "endStyle" : HoleEndStyle.BLIND, "holeDiameter" : 8 * mm, "holeDepth" : 1 * mm, "isTappedThrough" : true, "tappedDepth" : 12 * mm, "tapClearance" : 3, "locations" : qUnion([Q0, Q1, Q2, Q3, Q4]), "scope" : qUnion([Q5])});
        }
        {
            var Q0;
            Q0=makeQuery(id+"F36.opPattern","COPY",BODY,{"derivedFrom":makeQuery(id+"F35.opPattern","COPY",BODY,{"derivedFrom":makeQuery(id+"F32.opPattern","COPY",BODY,{"derivedFrom":makeQuery(id+"F31.opPattern","COPY",BODY,{"derivedFrom":makeQuery(id+"F29.opExtrude","SWEPT_BODY",BODY,{"disambiguationData":[OSD([sQuery(id+"F28.wireOp",EDGE,"E33")])]}),"instanceName":"1"}),"instanceName":"1"}),"instanceName":"1"}),"instanceName":"1"});
            var Q1;
            Q1=makeQuery(id+"F34.opPattern","COPY",BODY,{"derivedFrom":makeQuery(id+"F32.opPattern","COPY",BODY,{"derivedFrom":makeQuery(id+"F31.opPattern","COPY",BODY,{"derivedFrom":makeQuery(id+"F29.opExtrude","SWEPT_BODY",BODY,{"disambiguationData":[OSD([sQuery(id+"F28.wireOp",EDGE,"E33")])]}),"instanceName":"1"}),"instanceName":"1"}),"instanceName":"1"});
            var Q2;
            Q2=makeQuery(id+"F35.opPattern","COPY",BODY,{"derivedFrom":makeQuery(id+"F32.opPattern","COPY",BODY,{"derivedFrom":makeQuery(id+"F31.opPattern","COPY",BODY,{"derivedFrom":makeQuery(id+"F29.opExtrude","SWEPT_BODY",BODY,{"disambiguationData":[OSD([sQuery(id+"F28.wireOp",EDGE,"E33")])]}),"instanceName":"1"}),"instanceName":"1"}),"instanceName":"1"});
            var Q3;
            Q3=makeQuery(id+"F31.opPattern","COPY",BODY,{"derivedFrom":makeQuery(id+"F29.opExtrude","SWEPT_BODY",BODY,{"disambiguationData":[OSD([sQuery(id+"F28.wireOp",EDGE,"E33")])]}),"instanceName":"1"});
            transform(context, id + "F44", {"entities" : qUnion([Q0, Q1, Q2, Q3]), "transformType" : TransformType.TRANSLATION_3D, "dx" : 1 * mm, "dy" : 0 * mm, "dz" : 0 * mm, "makeCopy" : false});
        }
        {
            var Q0;
            Q0=makeQuery(id+"F29.opExtrude","SWEPT_BODY",BODY,{"disambiguationData":[OSD([sQuery(id+"F28.wireOp",EDGE,"E33")])]});
            transform(context, id + "F45", {"entities" : qUnion([Q0]), "transformType" : TransformType.TRANSLATION_3D, "dx" : 1 * mm, "dy" : 0 * mm, "dz" : 0 * mm, "makeCopy" : false});
        }
        {
            var Q0;
            Q0=makeQuery(id+"F6.opPattern","COPY",BODY,{"derivedFrom":makeQuery(id+"F3.opExtrude","SWEPT_BODY",BODY,{"disambiguationData":[OSD([sQuery(id+"F0.wireOp",EDGE,"E0"),sQuery(id+"F0.wireOp",EDGE,"E1"),sQuery(id+"F0.wireOp",EDGE,"E2"),sQuery(id+"F0.wireOp",EDGE,"E3"),sQuery(id+"F0.wireOp",EDGE,"E4"),sQuery(id+"F0.wireOp",EDGE,"E5"),sQuery(id+"F0.wireOp",EDGE,"E9.bottom"),sQuery(id+"F0.wireOp",EDGE,"E9.top"),sQuery(id+"F0.wireOp",EDGE,"E9.left"),sQuery(id+"F0.wireOp",EDGE,"E10"),sQuery(id+"F0.wireOp",EDGE,"E11"),sQuery(id+"F0.wireOp",EDGE,"E12"),sQuery(id+"F0.wireOp",EDGE,"E13.filletArc"),sQuery(id+"F0.wireOp",EDGE,"E14.filletArc")])]}),"instanceName":"1"});
            var Q1;
            Q1=makeQuery(id+"F5.opPattern","COPY",BODY,{"derivedFrom":makeQuery(id+"F3.opExtrude","SWEPT_BODY",BODY,{"disambiguationData":[OSD([sQuery(id+"F0.wireOp",EDGE,"E0"),sQuery(id+"F0.wireOp",EDGE,"E1"),sQuery(id+"F0.wireOp",EDGE,"E2"),sQuery(id+"F0.wireOp",EDGE,"E3"),sQuery(id+"F0.wireOp",EDGE,"E4"),sQuery(id+"F0.wireOp",EDGE,"E5"),sQuery(id+"F0.wireOp",EDGE,"E9.bottom"),sQuery(id+"F0.wireOp",EDGE,"E9.top"),sQuery(id+"F0.wireOp",EDGE,"E9.left"),sQuery(id+"F0.wireOp",EDGE,"E10"),sQuery(id+"F0.wireOp",EDGE,"E11"),sQuery(id+"F0.wireOp",EDGE,"E12"),sQuery(id+"F0.wireOp",EDGE,"E13.filletArc"),sQuery(id+"F0.wireOp",EDGE,"E14.filletArc")])]}),"instanceName":"1"});
            var Q2;
            Q2=makeQuery(id+"F3.opExtrude","SWEPT_BODY",BODY,{"disambiguationData":[OSD([sQuery(id+"F0.wireOp",EDGE,"E0"),sQuery(id+"F0.wireOp",EDGE,"E1"),sQuery(id+"F0.wireOp",EDGE,"E2"),sQuery(id+"F0.wireOp",EDGE,"E3"),sQuery(id+"F0.wireOp",EDGE,"E4"),sQuery(id+"F0.wireOp",EDGE,"E5"),sQuery(id+"F0.wireOp",EDGE,"E9.bottom"),sQuery(id+"F0.wireOp",EDGE,"E9.top"),sQuery(id+"F0.wireOp",EDGE,"E9.left"),sQuery(id+"F0.wireOp",EDGE,"E10"),sQuery(id+"F0.wireOp",EDGE,"E11"),sQuery(id+"F0.wireOp",EDGE,"E12"),sQuery(id+"F0.wireOp",EDGE,"E13.filletArc"),sQuery(id+"F0.wireOp",EDGE,"E14.filletArc")])]});
            var Q3;
            Q3=qCreatedBy(makeId("Right.planeOp"),FACE);
            mirror(context, id + "F46", {"entities" : qUnion([Q0, Q1, Q2]), "mirrorPlane" : qUnion([Q3])});
        }
        {
            var Q0;
            Q0=makeQuery(id+"F46.opPattern","COPY",BODY,{"derivedFrom":makeQuery(id+"F6.opPattern","COPY",BODY,{"derivedFrom":makeQuery(id+"F3.opExtrude","SWEPT_BODY",BODY,{"disambiguationData":[OSD([sQuery(id+"F0.wireOp",EDGE,"E0"),sQuery(id+"F0.wireOp",EDGE,"E1"),sQuery(id+"F0.wireOp",EDGE,"E2"),sQuery(id+"F0.wireOp",EDGE,"E3"),sQuery(id+"F0.wireOp",EDGE,"E4"),sQuery(id+"F0.wireOp",EDGE,"E5"),sQuery(id+"F0.wireOp",EDGE,"E9.bottom"),sQuery(id+"F0.wireOp",EDGE,"E9.top"),sQuery(id+"F0.wireOp",EDGE,"E9.left"),sQuery(id+"F0.wireOp",EDGE,"E10"),sQuery(id+"F0.wireOp",EDGE,"E11"),sQuery(id+"F0.wireOp",EDGE,"E12"),sQuery(id+"F0.wireOp",EDGE,"E13.filletArc"),sQuery(id+"F0.wireOp",EDGE,"E14.filletArc")])]}),"instanceName":"1"}),"instanceName":"1"});
            var Q1;
            Q1=makeQuery(id+"F46.opPattern","COPY",BODY,{"derivedFrom":makeQuery(id+"F3.opExtrude","SWEPT_BODY",BODY,{"disambiguationData":[OSD([sQuery(id+"F0.wireOp",EDGE,"E0"),sQuery(id+"F0.wireOp",EDGE,"E1"),sQuery(id+"F0.wireOp",EDGE,"E2"),sQuery(id+"F0.wireOp",EDGE,"E3"),sQuery(id+"F0.wireOp",EDGE,"E4"),sQuery(id+"F0.wireOp",EDGE,"E5"),sQuery(id+"F0.wireOp",EDGE,"E9.bottom"),sQuery(id+"F0.wireOp",EDGE,"E9.top"),sQuery(id+"F0.wireOp",EDGE,"E9.left"),sQuery(id+"F0.wireOp",EDGE,"E10"),sQuery(id+"F0.wireOp",EDGE,"E11"),sQuery(id+"F0.wireOp",EDGE,"E12"),sQuery(id+"F0.wireOp",EDGE,"E13.filletArc"),sQuery(id+"F0.wireOp",EDGE,"E14.filletArc")])]}),"instanceName":"1"});
            var Q2;
            Q2=makeQuery(id+"F46.opPattern","COPY",BODY,{"derivedFrom":makeQuery(id+"F5.opPattern","COPY",BODY,{"derivedFrom":makeQuery(id+"F3.opExtrude","SWEPT_BODY",BODY,{"disambiguationData":[OSD([sQuery(id+"F0.wireOp",EDGE,"E0"),sQuery(id+"F0.wireOp",EDGE,"E1"),sQuery(id+"F0.wireOp",EDGE,"E2"),sQuery(id+"F0.wireOp",EDGE,"E3"),sQuery(id+"F0.wireOp",EDGE,"E4"),sQuery(id+"F0.wireOp",EDGE,"E5"),sQuery(id+"F0.wireOp",EDGE,"E9.bottom"),sQuery(id+"F0.wireOp",EDGE,"E9.top"),sQuery(id+"F0.wireOp",EDGE,"E9.left"),sQuery(id+"F0.wireOp",EDGE,"E10"),sQuery(id+"F0.wireOp",EDGE,"E11"),sQuery(id+"F0.wireOp",EDGE,"E12"),sQuery(id+"F0.wireOp",EDGE,"E13.filletArc"),sQuery(id+"F0.wireOp",EDGE,"E14.filletArc")])]}),"instanceName":"1"}),"instanceName":"1"});
            transform(context, id + "F47", {"entities" : qUnion([Q0, Q1, Q2]), "transformType" : TransformType.TRANSLATION_3D, "dx" : -350 * mm, "dy" : 0 * mm, "dz" : 0 * mm, "makeCopy" : false});
        }
        {
            var Q0;
            Q0=makeQuery(id+"F29.opExtrude","SWEPT_BODY",BODY,{"disambiguationData":[OSD([sQuery(id+"F28.wireOp",EDGE,"E33")])]});
            transform(context, id + "F48", {"entities" : qUnion([Q0]), "transformType" : TransformType.TRANSLATION_3D, "dx" : -267 * mm, "dy" : 0 * mm, "dz" : 0 * mm, "makeCopy" : true});
        }
        {
            var Q0;
            Q0=makeQuery(id+"F35.opPattern","COPY",BODY,{"derivedFrom":makeQuery(id+"F32.opPattern","COPY",BODY,{"derivedFrom":makeQuery(id+"F31.opPattern","COPY",BODY,{"derivedFrom":makeQuery(id+"F29.opExtrude","SWEPT_BODY",BODY,{"disambiguationData":[OSD([sQuery(id+"F28.wireOp",EDGE,"E33")])]}),"instanceName":"1"}),"instanceName":"1"}),"instanceName":"1"});
            transform(context, id + "F49", {"entities" : qUnion([Q0]), "transformType" : TransformType.TRANSLATION_3D, "dx" : -267 * mm, "dy" : 0 * mm, "dz" : 0 * mm, "makeCopy" : true});
        }
        {
            var Q0;
            Q0=makeQuery(id+"F34.opPattern","COPY",BODY,{"derivedFrom":makeQuery(id+"F32.opPattern","COPY",BODY,{"derivedFrom":makeQuery(id+"F31.opPattern","COPY",BODY,{"derivedFrom":makeQuery(id+"F29.opExtrude","SWEPT_BODY",BODY,{"disambiguationData":[OSD([sQuery(id+"F28.wireOp",EDGE,"E33")])]}),"instanceName":"1"}),"instanceName":"1"}),"instanceName":"1"});
            transform(context, id + "F50", {"entities" : qUnion([Q0]), "transformType" : TransformType.TRANSLATION_3D, "dx" : -267 * mm, "dy" : 0 * mm, "dz" : 0 * mm, "makeCopy" : true});
        }
        {
            var Q0;
            Q0=makeQuery(id+"F32.opPattern","COPY",BODY,{"derivedFrom":makeQuery(id+"F31.opPattern","COPY",BODY,{"derivedFrom":makeQuery(id+"F29.opExtrude","SWEPT_BODY",BODY,{"disambiguationData":[OSD([sQuery(id+"F28.wireOp",EDGE,"E33")])]}),"instanceName":"1"}),"instanceName":"1"});
            transform(context, id + "F51", {"entities" : qUnion([Q0]), "transformType" : TransformType.TRANSLATION_3D, "dx" : -267 * mm, "dy" : 0 * mm, "dz" : 0 * mm, "makeCopy" : true});
        }
        {
            var Q0;
            Q0=makeQuery(id+"F31.opPattern","COPY",BODY,{"derivedFrom":makeQuery(id+"F29.opExtrude","SWEPT_BODY",BODY,{"disambiguationData":[OSD([sQuery(id+"F28.wireOp",EDGE,"E33")])]}),"instanceName":"1"});
            transform(context, id + "F52", {"entities" : qUnion([Q0]), "transformType" : TransformType.TRANSLATION_3D, "dx" : -267 * mm, "dy" : 0 * mm, "dz" : 0 * mm, "makeCopy" : true});
        }
        {
            var Q0;
            Q0=makeQuery(id+"F29.opExtrude","SWEPT_BODY",BODY,{"disambiguationData":[OSD([sQuery(id+"F28.wireOp",EDGE,"E33")])]});
            transform(context, id + "F53", {"entities" : qUnion([Q0]), "transformType" : TransformType.TRANSLATION_3D, "dx" : -267 * mm, "dy" : 0 * mm, "dz" : 0 * mm, "makeCopy" : true});
        }
        {
            var Q0;
            Q0=makeQuery(id+"F36.opPattern","COPY",BODY,{"derivedFrom":makeQuery(id+"F35.opPattern","COPY",BODY,{"derivedFrom":makeQuery(id+"F32.opPattern","COPY",BODY,{"derivedFrom":makeQuery(id+"F31.opPattern","COPY",BODY,{"derivedFrom":makeQuery(id+"F29.opExtrude","SWEPT_BODY",BODY,{"disambiguationData":[OSD([sQuery(id+"F28.wireOp",EDGE,"E33")])]}),"instanceName":"1"}),"instanceName":"1"}),"instanceName":"1"}),"instanceName":"1"});
            transform(context, id + "F54", {"entities" : qUnion([Q0]), "transformType" : TransformType.TRANSLATION_3D, "dx" : -267 * mm, "dy" : 0 * mm, "dz" : 0 * mm, "makeCopy" : true});
        }
    });
